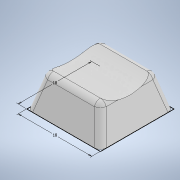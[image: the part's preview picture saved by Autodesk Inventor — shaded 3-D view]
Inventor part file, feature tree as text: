
AUTODESK INVENTOR PART (.ipt)
format: ipt  version: 2022 (Build 260153000, 153)  size: 190,976 bytes
history: native  units: in
note: dims shown in document units (in); Inventor stores cm internally (conversion verified against a paired STEP export)
features: extrude x5, sketch x5, fillet x1, plane x1
ambient origin geometry x8: Origin, YZ Plane, XZ Plane, XY Plane, X Axis, Y Axis, Z Axis, Center Point
bodies: Solid1 (feature_tree)
feature tree (12):
  extrude  "Extrusion1"  Depth=0.7087in
  fillet  "Fillet1"  Radius=0.315in
  plane  "Work Plane1"
  extrude  "Extrusion2"  Depth=0.4724in
  extrude  "Extrusion3"  Depth=0.6299in
  extrude  "Extrusion4"  Depth=0.1772in
  extrude  "Extrusion5"  Depth=0.1575in TaperAngle=0.0deg
  sketch  "Sketch1"  dims[d0=0.7087in d1=0.7087in d2=0.315in d3=-0.1031in]
  sketch  "Sketch2"  dims[d4=0.0591in d5=0.4724in]
  sketch  "Sketch3"  dims[d6=0.0in d7=0.0in d8=0.6299in]
  sketch  "Sketch4"  dims[d9=0.6299in d10=0.1772in d11=-0.1031in]
  sketch  "Sketch5"  dims[d12=0.2185in d13=0.1575in d14=0.0in d15=0.0472in d16=0.1634in d17=0.1634in d18=0.0472in d19=0.0118in d20=0.1575in d21=0.0in]
